# Revit family: Internal block_36__160_FC
name_source: partatom
category: Оборудование
units: mm (PartAtom-declared; Revit-internal decimal feet)

## family parameters
Всегда вертикально = Да
Классификация = Нет
На основе рабочей плоскости = Нет
Общий = Нет
При загрузке вырезать с полостями = Нет
Размер круглого соединителя = Использовать диаметр
Тип детали = Нормальный
Точка принадлежности помещению = Нет

## types (9) — shared parameters
00_20_Manufacturer = BLAUBERG
00_20_Name = Internal block
B = 675 мм
C = 235 мм
Casing Material = Plastic white
Grid Material = Mesh, steel, painted,  white
Height = 870 мм
Length = 1150 мм
Load Classification = HVAC
Maintenance zone material = <По категории>
Maximum Air Flow = 0.0 л/с
Width = 528 мм
r = 60 мм
r1 = 300 мм
Изготовитель = BLAUBERG
zero-valued in all types: Отметка по умолчанию

## per-type parameters (varying)
| type | A | Power | Weight |
| BLHV-36-I-FC-AC/1R1A | 1050 мм | 90 Вт | 26.50 кг |
| BLHV-160-I-FC-AC/1R1A | 1670 мм | 200 Вт | 41.00 кг |
| BLHV-45-I-FC-AC/1R1A | 1050 мм | 90 Вт | 26.50 кг |
| BLHV-56-I-FC-AC/1R1A | 1050 мм | 90 Вт | 26.50 кг |
| BLHV-71-I-FC-DC/1R1A | 1300 мм | 100 Вт | 32.50 кг |
| BLHV-80-I-FC-AC/1R1A | 1300 мм | 100 Вт | 32.50 кг |
| BLHV-90-I-FC-AC/1R1A | 1670 мм | 200 Вт | 41.00 кг |
| BLHV-112-I-FC-AC/1R1A | 1670 мм | 200 Вт | 41.00 кг |
| BLHV-140-I-FC-AC/1R1A | 1670 мм | 200 Вт | 41.00 кг |

note: column(s) folded — value = type name in every type: 00_20_Type
